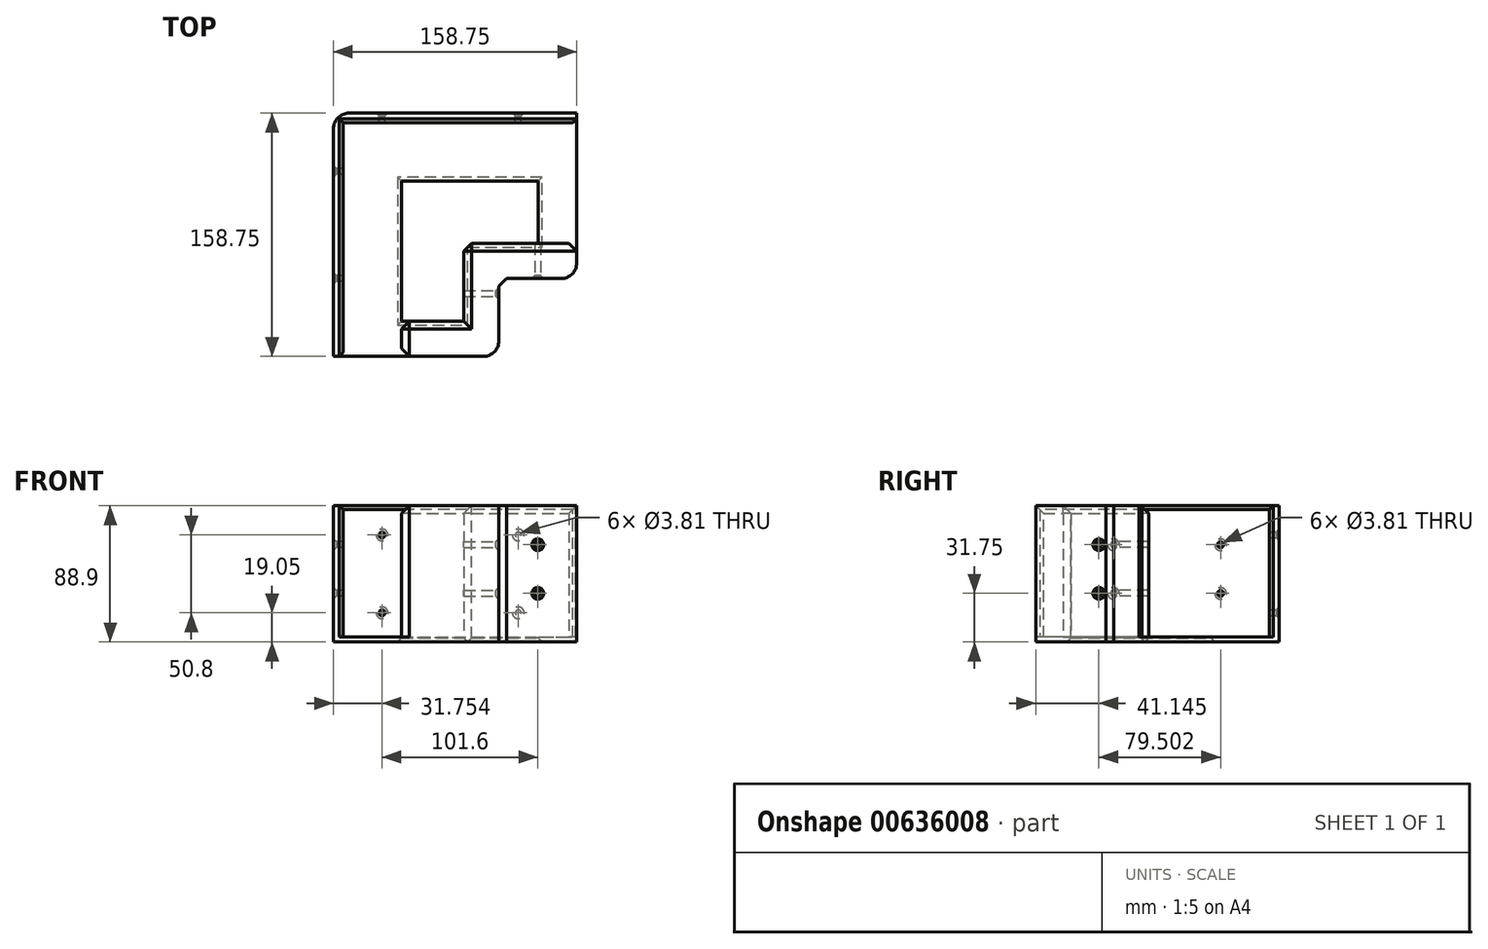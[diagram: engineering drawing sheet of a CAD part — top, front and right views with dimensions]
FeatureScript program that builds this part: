
annotation { "Feature Type Name" : "Feature", "Feature Type Description" : "" }
export const myFeature = defineFeature(function(context is Context, id is Id, definition is map)
    precondition{}
    {
        {
            var Q0;
            Q0=qCreatedBy(makeId("Top.planeOp"),FACE);
            var sketch = newSketch(context, id + "F0", { "sketchPlane" : qUnion([Q0])});
            skLineSegment(sketch, "E0.bottom", {"start": v(-359.38, 19.35) * mm, "end": v(-206.98, 19.35) * mm});
            skLineSegment(sketch, "E0.top", {"start": v(-359.38, -133.05) * mm, "end": v(-257.78, -133.05) * mm});
            skLineSegment(sketch, "E0.left", {"start": v(-359.38, 19.35) * mm, "end": v(-359.38, -133.05) * mm});
            skLineSegment(sketch, "E0.right", {"start": v(-206.98, 19.35) * mm, "end": v(-206.98, -82.25) * mm});
            skLineSegment(sketch, "E1.0", {"start": v(-365.73, 25.7) * mm, "end": v(-206.98, 25.7) * mm});
            skLineSegment(sketch, "E1.1", {"start": v(-365.73, 25.7) * mm, "end": v(-365.73, -133.05) * mm});
            skLineSegment(sketch, "E2.0", {"start": v(-280.64, -59.4) * mm, "end": v(-280.64, -110.2) * mm});
            skLineSegment(sketch, "E3.0", {"start": v(-321.28, -110.2) * mm, "end": v(-280.64, -110.2) * mm});
            skLineSegment(sketch, "E4", {"start": v(-321.28, -110.2) * mm, "end": v(-321.28, -133.05) * mm});
            skLineSegment(sketch, "E5", {"start": v(-280.64, -59.4) * mm, "end": v(-206.98, -59.4) * mm});
            skLineSegment(sketch, "E6", {"start": v(-206.98, 19.35) * mm, "end": v(-206.98, 25.7) * mm});
            skLineSegment(sketch, "E7", {"start": v(-359.38, -133.05) * mm, "end": v(-365.73, -133.05) * mm});
            skPoint(sketch, "E7.endSnap0", {"position": v(-365.73, -55.84) * mm});
            skPoint(sketch, "E8.orphan", {"position": v(-365.73, -137.37) * mm});
            skPoint(sketch, "E9.end.orphan", {"position": v(-280.64, -133.05) * mm});
            skLineSegment(sketch, "E10.0", {"start": v(-257.78, -82.25) * mm, "end": v(-257.78, -133.05) * mm});
            skLineSegment(sketch, "E11.0", {"start": v(-257.78, -82.25) * mm, "end": v(-206.98, -82.25) * mm});
            skLineSegment(sketch, "E12", {"start": v(-321.28, -110.2) * mm, "end": v(-321.28, -18.75) * mm});
            skLineSegment(sketch, "E13.0", {"start": v(-232.38, -59.4) * mm, "end": v(-232.38, -18.75) * mm});
            skLineSegment(sketch, "E14.0", {"start": v(-232.16, -59.4) * mm, "end": v(-232.16, -18.75) * mm});
            skLineSegment(sketch, "E15", {"start": v(-321.28, -18.75) * mm, "end": v(-232.16, -18.75) * mm});
            skSolve(sketch);
        }
        {
            var Q0;
            {var subQ4=sQuery(id+"F0.wireOp",EDGE,"E0.bottom");Q0=makeQuery(id+"F0.imprint","IMPRINT",FACE,{"disambiguationData":[TD([[makeQuery(id+"F0.imprint","IMPRINT",EDGE,{"derivedFrom":subQ4}),-1.0]])]});}
            extrude(context, id + "F1", {"entities" : qUnion([Q0]), "depth" : 3.17 * mm, "offsetDistance" : 25.4 * mm});
        }
        {
            var Q0;
            Q0=makeQuery(id+"F0.imprint","IMPRINT",FACE,{"disambiguationData":[TD([[makeQuery(id+"F0.imprint","IMPRINT",EDGE,{"derivedFrom":sQuery(id+"F0.wireOp",EDGE,"E3.0")}),-1.0]])]});
            var Q1;
            Q1=makeQuery(id+"F0.imprint","IMPRINT",FACE,{"disambiguationData":[TD([[makeQuery(id+"F0.imprint","IMPRINT",EDGE,{"derivedFrom":sQuery(id+"F0.wireOp",EDGE,"E0.bottom")}),1.0]])]});
            extrude(context, id + "F2", {"entities" : qUnion([Q0, Q1]), "operationType" : NewBodyOperationType.ADD, "depth" : 88.9 * mm, "offsetDistance" : 25.4 * mm});
        }
        {
            var Q0;
            Q0=makeQuery(id+"F2.opExtrude","SWEPT_FACE",FACE,{"disambiguationData":[OSD([sQuery(id+"F0.wireOp",EDGE,"E11.0")])]});
            var sketch = newSketch(context, id + "F3", { "sketchPlane" : qUnion([Q0])});
            skLineSegment(sketch, "E16.0", {"start": v(-257.78, 63.5) * mm, "end": v(-206.98, 63.5) * mm});
            skLineSegment(sketch, "E17.0", {"start": v(-257.78, 31.75) * mm, "end": v(-206.98, 31.75) * mm});
            skCircle(sketch, "E18", {"center": v(-232.38, 63.5) * mm, "radius": 2.22 * mm});
            skCircle(sketch, "E19", {"center": v(-232.38, 31.75) * mm, "radius": 2.22 * mm});
            skSolve(sketch);
        }
        {
            var Q0;
            Q0=sQuery(id+"F3.wireOp",VERTEX,"E18.center");
            var Q1;
            Q1=sQuery(id+"F3.wireOp",VERTEX,"E19.center");
            var Q2;
            Q2=makeQuery(id+"F1.opExtrude","SWEPT_BODY",BODY,{"disambiguationData":[OSD([sQuery(id+"F0.wireOp",EDGE,"E0.bottom"),sQuery(id+"F0.wireOp",EDGE,"E0.top"),sQuery(id+"F0.wireOp",EDGE,"E0.left"),sQuery(id+"F0.wireOp",EDGE,"E0.right"),sQuery(id+"F0.wireOp",EDGE,"E3.0"),sQuery(id+"F0.wireOp",EDGE,"E4"),sQuery(id+"F0.wireOp",EDGE,"E5"),sQuery(id+"F0.wireOp",EDGE,"E2.0")])]});
            hole(context, id + "F4", {"style" : HoleStyle.C_SINK, "endStyle" : HoleEndStyle.BLIND, "holeDiameter" : 3.8 * mm, "cSinkDiameter" : 7.62 * mm, "cSinkAngle" : 90 * degree, "majorDiameter" : 6.35 * mm, "holeDepth" : 25.4 * mm, "isTappedThrough" : true, "tappedDepth" : 12.7 * mm, "tapClearance" : 3, "locations" : qUnion([Q0, Q1]), "scope" : qUnion([Q2])});
        }
        {
            var Q0;
            Q0=makeQuery(id+"F2.opExtrude","SWEPT_FACE",FACE,{"disambiguationData":[OSD([sQuery(id+"F0.wireOp",EDGE,"E10.0")])]});
            var sketch = newSketch(context, id + "F5", { "sketchPlane" : qUnion([Q0])});
            skLineSegment(sketch, "E20.0", {"start": v(-82.25, 63.5) * mm, "end": v(-133.05, 63.5) * mm});
            skLineSegment(sketch, "E21.0", {"start": v(-82.25, 31.75) * mm, "end": v(-133.05, 31.75) * mm});
            skLineSegment(sketch, "E22.0", {"start": v(-91.9, 63.5) * mm, "end": v(-91.9, 31.75) * mm});
            skCircle(sketch, "E23", {"center": v(-91.9, 63.5) * mm, "radius": 2.22 * mm});
            skCircle(sketch, "E24", {"center": v(-91.9, 31.75) * mm, "radius": 2.22 * mm});
            skSolve(sketch);
        }
        {
            var Q0;
            Q0=sQuery(id+"F5.wireOp",VERTEX,"E23.center");
            var Q1;
            Q1=sQuery(id+"F5.wireOp",VERTEX,"E24.center");
            var Q2;
            Q2=makeQuery(id+"F1.opExtrude","SWEPT_BODY",BODY,{"disambiguationData":[OSD([sQuery(id+"F0.wireOp",EDGE,"E0.bottom"),sQuery(id+"F0.wireOp",EDGE,"E0.top"),sQuery(id+"F0.wireOp",EDGE,"E0.left"),sQuery(id+"F0.wireOp",EDGE,"E0.right"),sQuery(id+"F0.wireOp",EDGE,"E3.0"),sQuery(id+"F0.wireOp",EDGE,"E4"),sQuery(id+"F0.wireOp",EDGE,"E5"),sQuery(id+"F0.wireOp",EDGE,"E2.0")])]});
            hole(context, id + "F6", {"style" : HoleStyle.C_SINK, "endStyle" : HoleEndStyle.BLIND, "holeDiameter" : 3.8 * mm, "cSinkDiameter" : 7.62 * mm, "cSinkAngle" : 90 * degree, "majorDiameter" : 6.35 * mm, "holeDepth" : 25.4 * mm, "isTappedThrough" : true, "tappedDepth" : 12.7 * mm, "tapClearance" : 3, "locations" : qUnion([Q0, Q1]), "scope" : qUnion([Q2])});
        }
        {
            var Q0;
            Q0=makeQuery(id+"F2.opExtrude","SWEPT_FACE",FACE,{"disambiguationData":[OSD([sQuery(id+"F0.wireOp",EDGE,"E1.1")])]});
            var sketch = newSketch(context, id + "F7", { "sketchPlane" : qUnion([Q0])});
            skCircle(sketch, "E25", {"center": v(12.4, 63.5) * mm, "radius": 2.22 * mm});
            skCircle(sketch, "E26", {"center": v(12.4, 31.75) * mm, "radius": 2.22 * mm});
            skCircle(sketch, "E27", {"center": v(82.25, 63.5) * mm, "radius": 2.22 * mm});
            skCircle(sketch, "E28", {"center": v(82.25, 31.75) * mm, "radius": 2.22 * mm});
            skSolve(sketch);
        }
        {
            var Q0;
            Q0=sQuery(id+"F7.wireOp",VERTEX,"E25.center");
            var Q1;
            Q1=sQuery(id+"F7.wireOp",VERTEX,"E27.center");
            var Q2;
            Q2=sQuery(id+"F7.wireOp",VERTEX,"E28.center");
            var Q3;
            Q3=sQuery(id+"F7.wireOp",VERTEX,"E26.center");
            var Q4;
            Q4=makeQuery(id+"F1.opExtrude","SWEPT_BODY",BODY,{"disambiguationData":[OSD([sQuery(id+"F0.wireOp",EDGE,"E0.bottom"),sQuery(id+"F0.wireOp",EDGE,"E0.top"),sQuery(id+"F0.wireOp",EDGE,"E0.left"),sQuery(id+"F0.wireOp",EDGE,"E0.right"),sQuery(id+"F0.wireOp",EDGE,"E3.0"),sQuery(id+"F0.wireOp",EDGE,"E4"),sQuery(id+"F0.wireOp",EDGE,"E5"),sQuery(id+"F0.wireOp",EDGE,"E2.0")])]});
            hole(context, id + "F8", {"style" : HoleStyle.C_SINK, "endStyle" : HoleEndStyle.BLIND, "holeDiameter" : 3.8 * mm, "cSinkDiameter" : 7.62 * mm, "cSinkAngle" : 90 * degree, "majorDiameter" : 6.35 * mm, "holeDepth" : 25.4 * mm, "isTappedThrough" : true, "tappedDepth" : 12.7 * mm, "tapClearance" : 3, "locations" : qUnion([Q0, Q1, Q2, Q3]), "scope" : qUnion([Q4])});
        }
        {
            var Q0;
            Q0=makeQuery(id+"F2.opExtrude","SWEPT_FACE",FACE,{"disambiguationData":[OSD([sQuery(id+"F0.wireOp",EDGE,"E1.0")])]});
            var sketch = newSketch(context, id + "F9", { "sketchPlane" : qUnion([Q0])});
            skLineSegment(sketch, "E29.0", {"start": v(365.73, 69.85) * mm, "end": v(206.98, 69.85) * mm});
            skLineSegment(sketch, "E30.0", {"start": v(365.73, 19.05) * mm, "end": v(206.98, 19.05) * mm});
            skLineSegment(sketch, "E31.0", {"start": v(245.08, 88.9) * mm, "end": v(245.08, 0) * mm});
            skLineSegment(sketch, "E32.0", {"start": v(333.98, 88.9) * mm, "end": v(333.98, 0) * mm});
            skCircle(sketch, "E33", {"center": v(245.08, 69.85) * mm, "radius": 2.22 * mm});
            skCircle(sketch, "E34", {"center": v(245.08, 19.05) * mm, "radius": 2.22 * mm});
            skCircle(sketch, "E35", {"center": v(333.98, 69.85) * mm, "radius": 2.22 * mm});
            skCircle(sketch, "E36", {"center": v(333.98, 19.05) * mm, "radius": 2.22 * mm});
            skSolve(sketch);
        }
        {
            var Q0;
            Q0=sQuery(id+"F9.wireOp",VERTEX,"E33.center");
            var Q1;
            Q1=sQuery(id+"F9.wireOp",VERTEX,"E34.center");
            var Q2;
            Q2=sQuery(id+"F9.wireOp",VERTEX,"E36.center");
            var Q3;
            Q3=sQuery(id+"F9.wireOp",VERTEX,"E35.center");
            var Q4;
            Q4=makeQuery(id+"F1.opExtrude","SWEPT_BODY",BODY,{"disambiguationData":[OSD([sQuery(id+"F0.wireOp",EDGE,"E0.bottom"),sQuery(id+"F0.wireOp",EDGE,"E0.top"),sQuery(id+"F0.wireOp",EDGE,"E0.left"),sQuery(id+"F0.wireOp",EDGE,"E0.right"),sQuery(id+"F0.wireOp",EDGE,"E3.0"),sQuery(id+"F0.wireOp",EDGE,"E4"),sQuery(id+"F0.wireOp",EDGE,"E5"),sQuery(id+"F0.wireOp",EDGE,"E2.0")])]});
            hole(context, id + "F10", {"style" : HoleStyle.C_SINK, "endStyle" : HoleEndStyle.BLIND, "holeDiameter" : 3.8 * mm, "cSinkDiameter" : 7.62 * mm, "cSinkAngle" : 90 * degree, "majorDiameter" : 6.35 * mm, "holeDepth" : 25.4 * mm, "isTappedThrough" : true, "tappedDepth" : 12.7 * mm, "tapClearance" : 3, "locations" : qUnion([Q0, Q1, Q2, Q3]), "scope" : qUnion([Q4])});
        }
        {
            var Q0;
            {var subQ0=sQuery(id+"F0.wireOp",EDGE,"E3.0");var subQ1=sQuery(id+"F0.wireOp",EDGE,"E4");Q0=makeQuery(id+"F2.boolean.opBoolean","SPLIT",EDGE,{"disambiguationData":[topologyDisambiguationEdgeConnected([makeQuery(id+"F2.opExtrude","SWEPT_FACE",FACE,{"disambiguationData":[OSD([subQ1])]})])],"derivedFrom":makeQuery(id+"F2.opExtrude","SWEPT_EDGE",EDGE,{"disambiguationData":[OSD([subQ0,subQ1,sQuery(id+"F0.wireOp",EDGE,"E12")])]})});}
            var Q1;
            Q1=makeQuery(id+"F2.opExtrude","SWEPT_EDGE",EDGE,{"disambiguationData":[OSD([sQuery(id+"F0.wireOp",EDGE,"E0.top"),sQuery(id+"F0.wireOp",EDGE,"E4")])]});
            var Q2;
            Q2=makeQuery(id+"F2.opExtrude","SWEPT_EDGE",EDGE,{"disambiguationData":[OSD([sQuery(id+"F0.wireOp",EDGE,"E5"),sQuery(id+"F0.wireOp",EDGE,"E2.0"),sQuery(id+"F0.wireOp",EDGE,"OMfFkXrl-rnHp-J6tB-13Em-22fhUk422QXy")])]});
            var Q3;
            Q3=makeQuery(id+"F2.opExtrude","SWEPT_EDGE",EDGE,{"disambiguationData":[OSD([sQuery(id+"F0.wireOp",EDGE,"E10.0"),sQuery(id+"F0.wireOp",EDGE,"E11.0")])]});
            var Q4;
            Q4=makeQuery(id+"F2.opExtrude","SWEPT_EDGE",EDGE,{"disambiguationData":[OSD([sQuery(id+"F0.wireOp",EDGE,"E0.right"),sQuery(id+"F0.wireOp",EDGE,"E5")])]});
            var Q5;
            Q5=makeQuery(id+"F2.opExtrude","CAP_EDGE",EDGE,{"disambiguationData":[OSD([sQuery(id+"F0.wireOp",EDGE,"E3.0")])],"isStart":false});
            var Q6;
            Q6=makeQuery(id+"F2.opExtrude","CAP_EDGE",EDGE,{"disambiguationData":[OSD([sQuery(id+"F0.wireOp",EDGE,"E2.0")])],"isStart":false});
            var Q7;
            Q7=makeQuery(id+"F2.opExtrude","CAP_EDGE",EDGE,{"disambiguationData":[OSD([sQuery(id+"F0.wireOp",EDGE,"E5")])],"isStart":false});
            var Q8;
            Q8=makeQuery(id+"F2.opExtrude","CAP_EDGE",EDGE,{"disambiguationData":[OSD([sQuery(id+"F0.wireOp",EDGE,"E4")])],"isStart":false});
            chamfer(context, id + "F11", {"entities" : qUnion([Q0, Q1, Q2, Q3, Q4, Q5, Q6, Q7, Q8]), "width" : 5.08 * mm, "tangentPropagation" : true});
        }
        {
            var Q0;
            Q0=makeQuery(id+"F2.opExtrude","SWEPT_EDGE",EDGE,{"disambiguationData":[OSD([sQuery(id+"F0.wireOp",EDGE,"E0.top"),sQuery(id+"F0.wireOp",EDGE,"E10.0")])]});
            var Q1;
            Q1=makeQuery(id+"F2.opExtrude","SWEPT_EDGE",EDGE,{"disambiguationData":[OSD([sQuery(id+"F0.wireOp",EDGE,"E0.right"),sQuery(id+"F0.wireOp",EDGE,"E11.0")])]});
            var Q2;
            Q2=makeQuery(id+"F2.opExtrude","SWEPT_EDGE",EDGE,{"disambiguationData":[OSD([sQuery(id+"F0.wireOp",EDGE,"E1.0"),sQuery(id+"F0.wireOp",EDGE,"E1.1")])]});
            fillet(context, id + "F12", {"entities" : qUnion([Q0, Q1, Q2]), "radius" : 10.16 * mm, "tangentPropagation" : true, "allowEdgeOverflow" : false});
        }
        {
            var Q0;
            Q0=makeQuery(id+"F1.opExtrude","CAP_EDGE",EDGE,{"disambiguationData":[OSD([sQuery(id+"F0.wireOp",EDGE,"E4"),sQuery(id+"F0.wireOp",EDGE,"E12")])],"isStart":true});
            var Q1;
            Q1=makeQuery(id+"F1.opExtrude","CAP_EDGE",EDGE,{"disambiguationData":[OSD([sQuery(id+"F0.wireOp",EDGE,"ceec1e2b-4ce7-4a13-941b-c3b55e0174a0.0")])],"isStart":true});
            var Q2;
            Q2=makeQuery(id+"F2.boolean.opBoolean","MERGE",EDGE,{"derivedFrom":[makeQuery(id+"F1.opExtrude","CAP_EDGE",EDGE,{"disambiguationData":[OSD([sQuery(id+"F0.wireOp",EDGE,"OMfFkXrl-rnHp-J6tB-13Em-22fhUk422QXy")])],"isStart":true}),makeQuery(id+"F2.opExtrude","CAP_EDGE",EDGE,{"disambiguationData":[OSD([sQuery(id+"F0.wireOp",EDGE,"E2.0")])],"isStart":true})]});
            var Q3;
            Q3=makeQuery(id+"F2.opExtrude","CAP_EDGE",EDGE,{"disambiguationData":[OSD([sQuery(id+"F0.wireOp",EDGE,"E3.0")])],"isStart":true});
            var Q4;
            Q4=makeQuery(id+"F2.opExtrude","CAP_EDGE",EDGE,{"disambiguationData":[OSD([sQuery(id+"F0.wireOp",EDGE,"E0.bottom")])],"isStart":false});
            var Q5;
            Q5=makeQuery(id+"F2.opExtrude","CAP_EDGE",EDGE,{"disambiguationData":[OSD([sQuery(id+"F0.wireOp",EDGE,"E0.left")])],"isStart":false});
            var Q6;
            {var subQ0=sQuery(id+"F0.wireOp",EDGE,"E0.right");Q6=makeQuery(id+"F11.opChamfer","BLEND_EDGE",EDGE,{"blendedFrom":[makeQuery(id+"F2.opExtrude","SWEPT_EDGE",EDGE,{"disambiguationData":[OSD([subQ0,sQuery(id+"F0.wireOp",EDGE,"E5")])]}),makeQuery(id+"F2.boolean.opBoolean","MERGE",FACE,{"derivedFrom":[makeQuery(id+"F1.opExtrude","SWEPT_FACE",FACE,{"disambiguationData":[OSD([subQ0])]}),makeQuery(id+"F2.opExtrude","SWEPT_FACE",FACE,{"disambiguationData":[OSD([subQ0])]}),makeQuery(id+"F2.opExtrude","SWEPT_FACE",FACE,{"disambiguationData":[OSD([sQuery(id+"F0.wireOp",EDGE,"E6")])]})]})],"blendedInto":[makeQuery(id+"F2.boolean.opBoolean","MERGE",FACE,{"derivedFrom":[makeQuery(id+"F1.opExtrude","SWEPT_FACE",FACE,{"disambiguationData":[OSD([subQ0])]}),makeQuery(id+"F2.opExtrude","SWEPT_FACE",FACE,{"disambiguationData":[OSD([subQ0])]}),makeQuery(id+"F2.opExtrude","SWEPT_FACE",FACE,{"disambiguationData":[OSD([sQuery(id+"F0.wireOp",EDGE,"E6")])]})]})]});}
            var Q7;
            Q7=makeQuery(id+"F2.opExtrude","SWEPT_EDGE",EDGE,{"disambiguationData":[OSD([sQuery(id+"F0.wireOp",EDGE,"E0.bottom"),sQuery(id+"F0.wireOp",EDGE,"E0.right"),sQuery(id+"F0.wireOp",EDGE,"E6")])]});
            var Q8;
            Q8=makeQuery(id+"F2.opExtrude","SWEPT_EDGE",EDGE,{"disambiguationData":[OSD([sQuery(id+"F0.wireOp",EDGE,"E0.top"),sQuery(id+"F0.wireOp",EDGE,"E0.left"),sQuery(id+"F0.wireOp",EDGE,"E7")])]});
            var Q9;
            Q9=makeQuery(id+"F2.opExtrude","CAP_EDGE",EDGE,{"disambiguationData":[OSD([sQuery(id+"F0.wireOp",EDGE,"E5")])],"isStart":true});
            var Q10;
            Q10=makeQuery(id+"F1.opExtrude","CAP_EDGE",EDGE,{"disambiguationData":[OSD([sQuery(id+"F0.wireOp",EDGE,"E14.0")])],"isStart":true});
            var Q11;
            Q11=makeQuery(id+"F1.opExtrude","CAP_EDGE",EDGE,{"disambiguationData":[OSD([sQuery(id+"F0.wireOp",EDGE,"E15")])],"isStart":true});
            var Q12;
            Q12=makeQuery(id+"F2.opExtrude","CAP_EDGE",EDGE,{"disambiguationData":[OSD([sQuery(id+"F0.wireOp",EDGE,"E2.0")])],"isStart":true});
            chamfer(context, id + "F13", {"entities" : qUnion([Q0, Q1, Q2, Q3, Q4, Q5, Q6, Q7, Q8, Q9, Q10, Q11, Q12]), "width" : 2.54 * mm, "tangentPropagation" : true});
        }
        {
            var Q0;
            Q0=sQuery(id+"F9.wireOp",VERTEX,"E33.center");
            var Q1;
            Q1=sQuery(id+"F9.wireOp",VERTEX,"E34.center");
            var Q2;
            Q2=sQuery(id+"F9.wireOp",VERTEX,"E35.center");
            var Q3;
            Q3=sQuery(id+"F9.wireOp",VERTEX,"E36.center");
            var Q4;
            Q4=makeQuery(id+"F1.opExtrude","SWEPT_BODY",BODY,{"disambiguationData":[OSD([sQuery(id+"F0.wireOp",EDGE,"E0.bottom"),sQuery(id+"F0.wireOp",EDGE,"E0.top"),sQuery(id+"F0.wireOp",EDGE,"E0.left"),sQuery(id+"F0.wireOp",EDGE,"E0.right"),sQuery(id+"F0.wireOp",EDGE,"E3.0"),sQuery(id+"F0.wireOp",EDGE,"E4"),sQuery(id+"F0.wireOp",EDGE,"E5"),sQuery(id+"F0.wireOp",EDGE,"E2.0")])]});
            hole(context, id + "F14", {"style" : HoleStyle.C_SINK, "endStyle" : HoleEndStyle.BLIND, "holeDiameter" : 3.8 * mm, "cSinkDiameter" : 7.62 * mm, "cSinkAngle" : 90 * degree, "majorDiameter" : 6.35 * mm, "holeDepth" : 25.4 * mm, "isTappedThrough" : true, "tappedDepth" : 12.7 * mm, "tapClearance" : 3, "locations" : qUnion([Q0, Q1, Q2, Q3]), "scope" : qUnion([Q4])});
        }
    });
